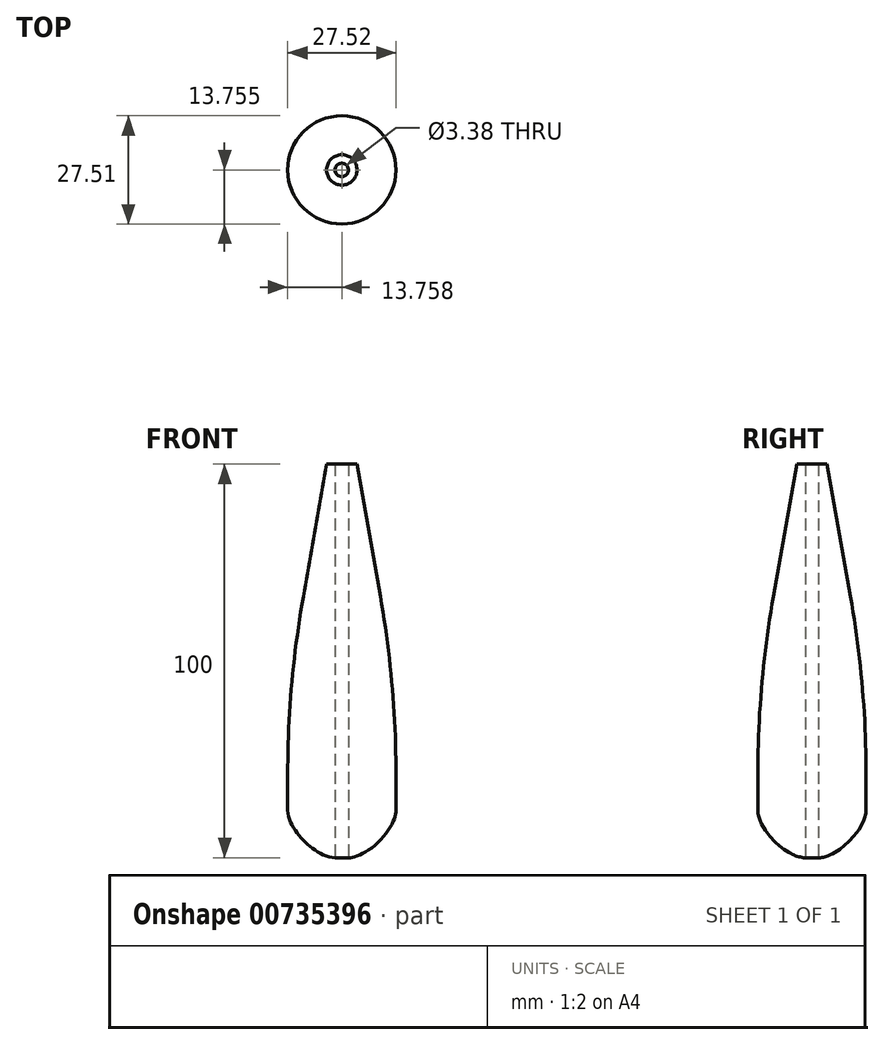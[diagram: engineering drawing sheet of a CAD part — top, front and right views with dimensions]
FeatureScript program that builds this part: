
annotation { "Feature Type Name" : "Feature", "Feature Type Description" : "" }
export const myFeature = defineFeature(function(context is Context, id is Id, definition is map)
    precondition{}
    {
        {
            var Q0;
            Q0=qCreatedBy(makeId("Top.planeOp"),FACE);
            var sketch = newSketch(context, id + "F0", { "sketchPlane" : qUnion([Q0])});
            skCircle(sketch, "E0", {"center": v(-55.12, -44.32) * mm, "radius": 13.76 * mm});
            skSolve(sketch);
        }
        {
            var Q0;
            Q0=makeQuery(id+"F0.imprint","IMPRINT",FACE,{"disambiguationData":[TD([[makeQuery(id+"F0.imprint","IMPRINT",EDGE,{"derivedFrom":sQuery(id+"F0.wireOp",EDGE,"E0")}),1.0]])]});
            extrude(context, id + "F1", {"entities" : qUnion([Q0]), "depth" : 100 * mm, "offsetDistance" : 25 * mm});
        }
        {
            var Q0;
            Q0=makeQuery(id+"F1.opExtrude","CAP_FACE",FACE,{"disambiguationData":[OSD([sQuery(id+"F0.wireOp",EDGE,"E0")])],"isStart":true});
            fillet(context, id + "F2", {"entities" : qUnion([Q0]), "crossSection" : FilletCrossSection.CONIC, "radius" : 12.07 * mm, "rho" : .3, "defaultsChanged" : false, "vertexSettings" : [], "allowEdgeOverflow" : false});
        }
        {
            var Q0;
            Q0=makeQuery(id+"F1.opExtrude","CAP_FACE",FACE,{"disambiguationData":[OSD([sQuery(id+"F0.wireOp",EDGE,"E0")])],"isStart":true});
            extrude(context, id + "F3", {"entities" : qUnion([Q0]), "operationType" : NewBodyOperationType.REMOVE, "endBound" : BoundingType.THROUGH_ALL, "oppositeDirection" : true, "depth" : 25 * mm, "offsetDistance" : 25 * mm});
        }
        {
            var Q0;
            Q0=makeQuery(id+"F1.opExtrude","CAP_EDGE",EDGE,{"disambiguationData":[OSD([sQuery(id+"F0.wireOp",EDGE,"E0")])],"isStart":false});
            chamfer(context, id + "F4", {"entities" : qUnion([Q0]), "chamferType" : ChamferType.OFFSET_ANGLE, "width" : 9.9 * mm, "oppositeDirection" : false, "angle" : 80 * degree, "tangentPropagation" : true});
        }
        {
            var Q0;
            {var subQ0=sQuery(id+"F0.wireOp",EDGE,"E0");Q0=makeQuery(id+"F4.opChamfer","BLEND_EDGE",EDGE,{"blendedFrom":[makeQuery(id+"F1.opExtrude","CAP_EDGE",EDGE,{"disambiguationData":[OSD([subQ0])],"isStart":false}),makeQuery(id+"F1.opExtrude","SWEPT_FACE",FACE,{"disambiguationData":[OSD([subQ0])]})],"blendedInto":[makeQuery(id+"F1.opExtrude","SWEPT_FACE",FACE,{"disambiguationData":[OSD([subQ0])]})]});}
            fillet(context, id + "F5", {"entities" : qUnion([Q0]), "tangentPropagation" : true, "radius" : 261.8 * mm, "defaultsChanged" : true, "vertexSettings" : [], "allowEdgeOverflow" : false});
        }
    });
